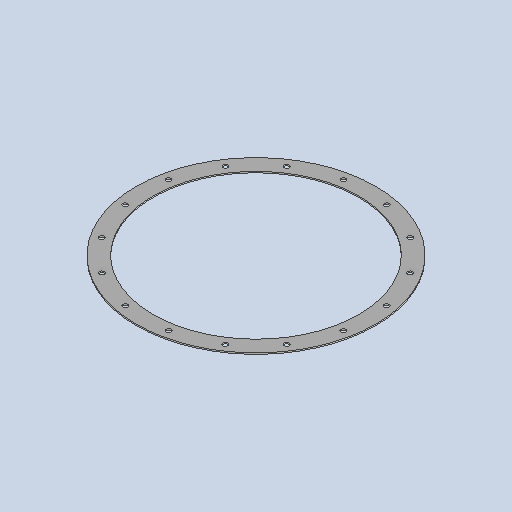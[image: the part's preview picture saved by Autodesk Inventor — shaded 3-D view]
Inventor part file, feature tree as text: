
AUTODESK INVENTOR PART (.ipt)
format: ipt  version: 2025 (Build 290162010, 162A)  size: 178,688 bytes
history: native  units: mm
features: sketch x3, extrude x2, other x2, sheet_metal_op x1, pattern_circular x1, projected_geometry x1
ambient origin geometry x8: Origin, YZ Plane, XZ Plane, XY Plane, X Axis, Y Axis, Z Axis, Center Point
bodies: Solid1 (feature_tree)
feature tree (10):
  sheet_metal_op  "Face1"
  extrude  "Extrusion1"  TaperAngle=0.0deg  [1 undecoded]
  extrude  "Extrusion2"  Depth=40.0mm
  pattern_circular  "Circular Pattern2"  [2 undecoded]
  sketch  "Sketch1"  dims[d2=3.0mm d4=0.0mm d5=0.0mm]
  other  "Plate1"
  sketch  "Sketch2"  dims[d9=530.0mm d11=40.0mm]
  projected_geometry  "Projected Loop1"
  sketch  "Sketch3"  dims[d20=1.963495mm d21=12.0mm d23=5.0mm d24=10.0mm d25=0.0mm d26=0.0mm d27=160.0mm d28=360.0deg]
  other  "Definition1"
note: 3 required parameter values undecoded (feature->parameter linkage not recoverable at this tier; creation-order binding heuristic only, values carry confidence <= 0.55)
